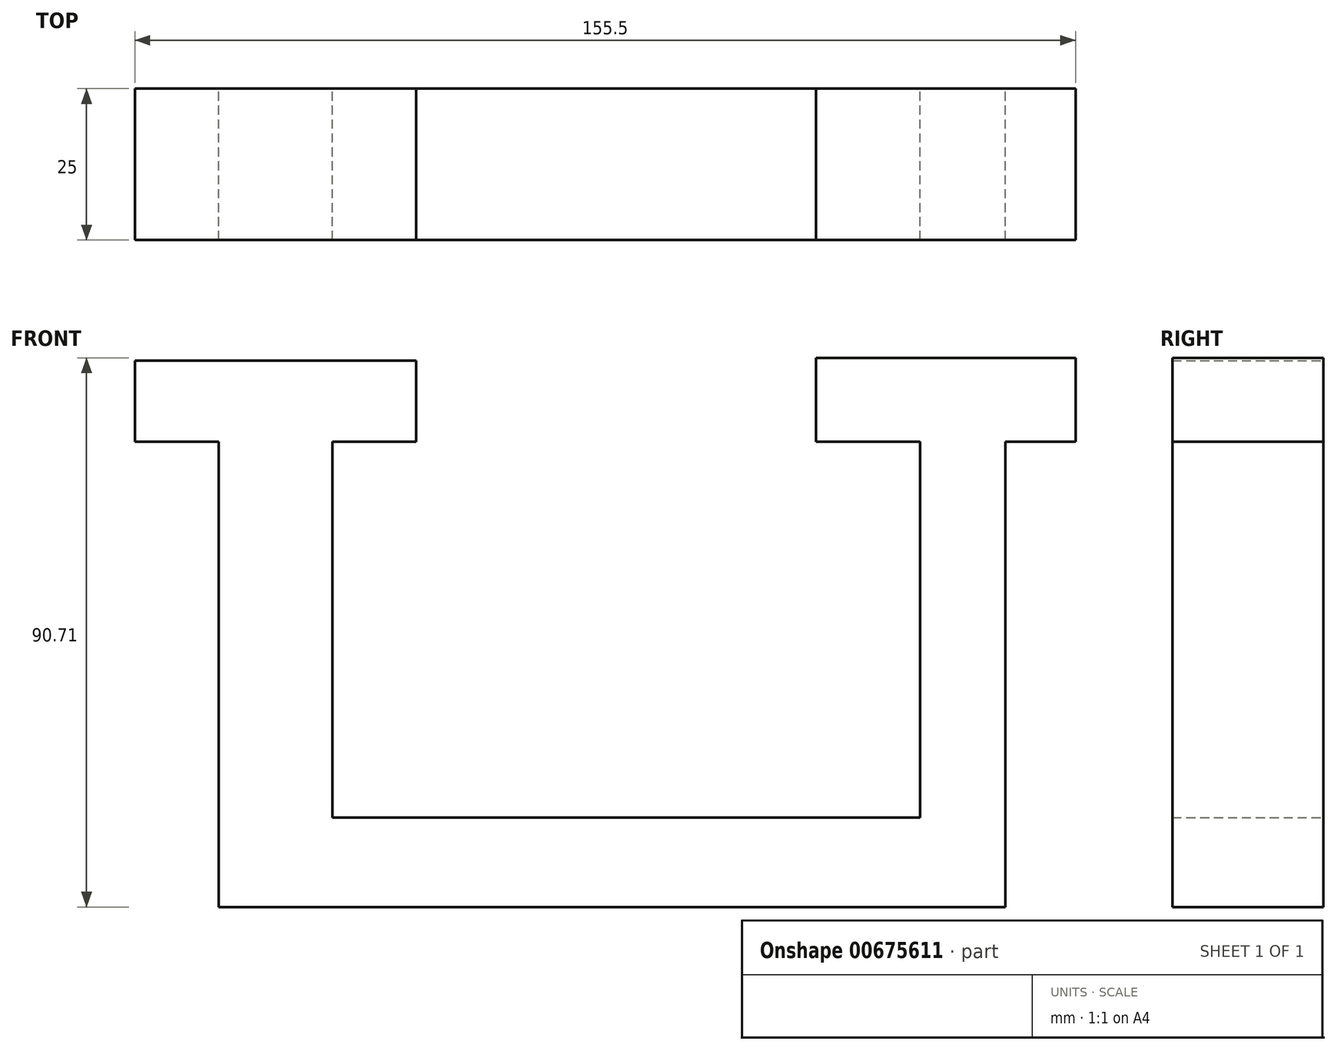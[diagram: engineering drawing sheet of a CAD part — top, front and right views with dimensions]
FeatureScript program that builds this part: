
annotation { "Feature Type Name" : "Feature", "Feature Type Description" : "" }
export const myFeature = defineFeature(function(context is Context, id is Id, definition is map)
    precondition{}
    {
        {
            var Q0;
            Q0=qCreatedBy(makeId("Front.planeOp"),FACE);
            var sketch = newSketch(context, id + "F0", { "sketchPlane" : qUnion([Q0])});
            skLineSegment(sketch, "E0", {"start": v(-129.8, 48.05) * mm, "end": v(-83.34, 48.05) * mm});
            skLineSegment(sketch, "E1", {"start": v(-83.34, 48.05) * mm, "end": v(-83.34, 34.62) * mm});
            skLineSegment(sketch, "E2", {"start": v(-83.34, 34.62) * mm, "end": v(-97.19, 34.62) * mm});
            skLineSegment(sketch, "E3", {"start": v(-97.19, 34.62) * mm, "end": v(-97.19, -27.5) * mm});
            skLineSegment(sketch, "E4", {"start": v(-97.19, -27.5) * mm, "end": v(0, -27.5) * mm});
            skLineSegment(sketch, "E5", {"start": v(0, -27.5) * mm, "end": v(0, 34.62) * mm});
            skLineSegment(sketch, "E6", {"start": v(0, 34.62) * mm, "end": v(-17.2, 34.62) * mm});
            skLineSegment(sketch, "E7", {"start": v(-17.2, 34.62) * mm, "end": v(-17.2, 48.47) * mm});
            skLineSegment(sketch, "E8", {"start": v(-17.2, 48.47) * mm, "end": v(25.7, 48.47) * mm});
            skLineSegment(sketch, "E9", {"start": v(25.7, 48.47) * mm, "end": v(25.7, 34.62) * mm});
            skLineSegment(sketch, "E10", {"start": v(25.7, 34.62) * mm, "end": v(14.08, 34.62) * mm});
            skLineSegment(sketch, "E11", {"start": v(14.08, 34.62) * mm, "end": v(14.08, -42.24) * mm});
            skLineSegment(sketch, "E12", {"start": v(14.08, -42.24) * mm, "end": v(-115.95, -42.24) * mm});
            skLineSegment(sketch, "E13", {"start": v(-115.95, -42.24) * mm, "end": v(-115.95, 34.62) * mm});
            skLineSegment(sketch, "E14", {"start": v(-115.95, 34.62) * mm, "end": v(-129.8, 34.62) * mm});
            skLineSegment(sketch, "E15", {"start": v(-129.8, 34.62) * mm, "end": v(-129.8, 48.05) * mm});
            skSolve(sketch);
        }
        {
            var Q0;
            Q0 = qSketchRegion(id + "F0", true);
            extrude(context, id + "F1", {"entities" : qUnion([Q0]), "depth" : 25 * mm, "offsetDistance" : 25 * mm});
        }
    });
